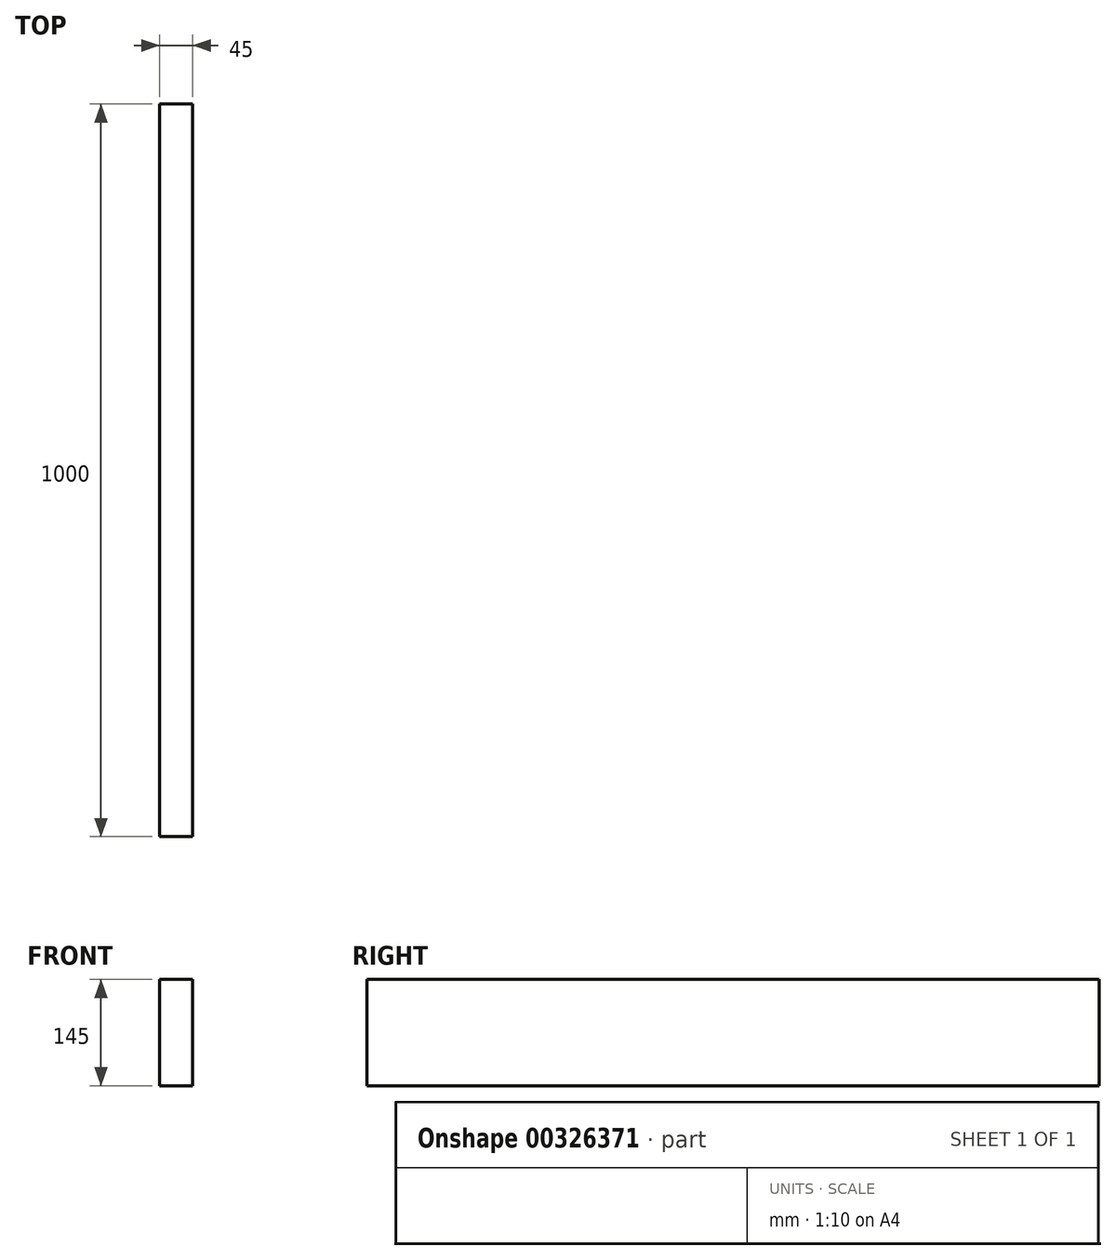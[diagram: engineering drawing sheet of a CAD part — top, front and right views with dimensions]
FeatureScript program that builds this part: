
annotation { "Feature Type Name" : "Feature", "Feature Type Description" : "" }
export const myFeature = defineFeature(function(context is Context, id is Id, definition is map)
    precondition{}
    {
        {
            var Q0;
            Q0=qCreatedBy(makeId("Front.planeOp"),FACE);
            var sketch = newSketch(context, id + "F0", { "sketchPlane" : qUnion([Q0])});
            skLineSegment(sketch, "E0.bottom", {"start": v(0, 0) * mm, "end": v(45, 0) * mm});
            skLineSegment(sketch, "E0.top", {"start": v(0, 145) * mm, "end": v(45, 145) * mm});
            skLineSegment(sketch, "E0.left", {"start": v(0, 0) * mm, "end": v(0, 145) * mm});
            skLineSegment(sketch, "E0.right", {"start": v(45, 0) * mm, "end": v(45, 145) * mm});
            skSolve(sketch);
        }
        {
            var Q0;
            Q0=makeQuery(id+"F0.imprint","IMPRINT",FACE,{"disambiguationData":[TD([[makeQuery(id+"F0.imprint","IMPRINT",EDGE,{"derivedFrom":sQuery(id+"F0.wireOp",EDGE,"E0.bottom")}),1.0]])]});
            extrude(context, id + "F1", {"entities" : qUnion([Q0]), "depth" : 1000 * mm});
        }
    });
